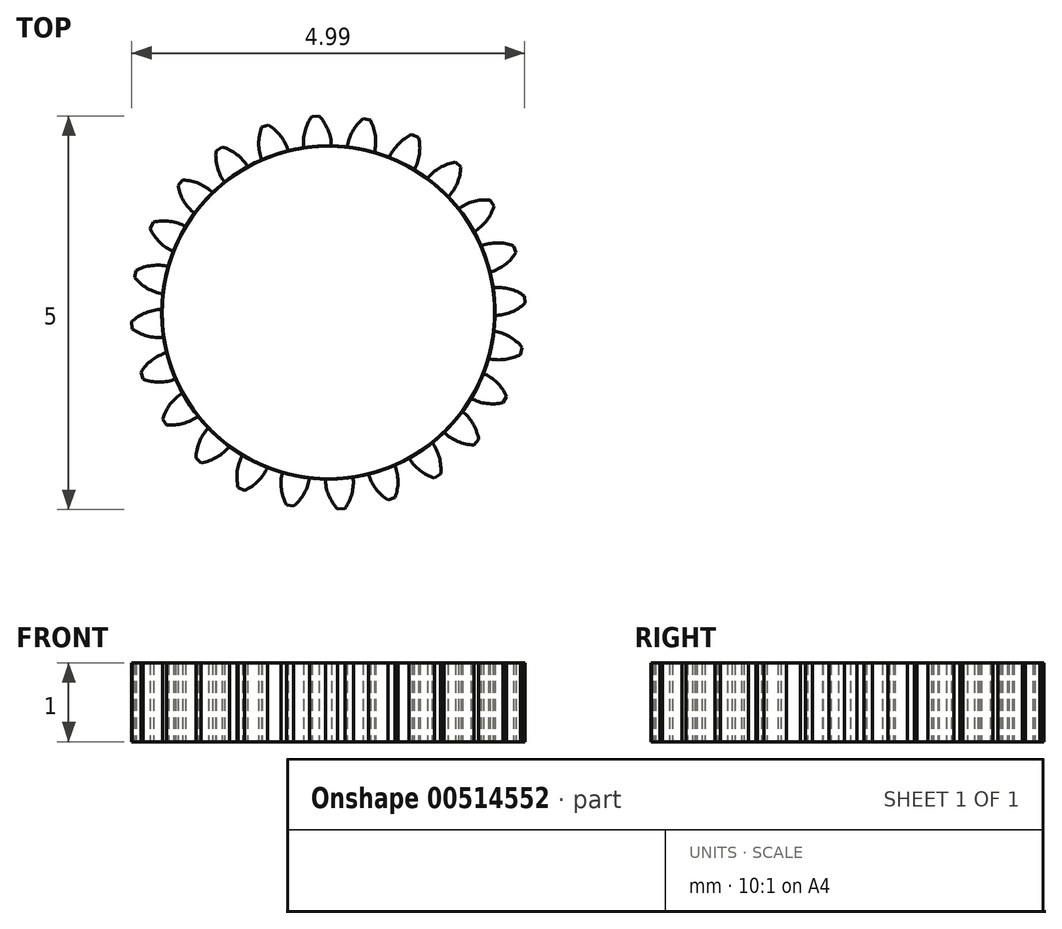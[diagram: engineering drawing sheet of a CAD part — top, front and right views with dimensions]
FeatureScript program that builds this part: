
annotation { "Feature Type Name" : "Feature", "Feature Type Description" : "" }
export const myFeature = defineFeature(function(context is Context, id is Id, definition is map)
    precondition{}
    {
        {
            var Q0;
            Q0=qCreatedBy(makeId("Top.planeOp"),FACE);
            var sketch = newSketch(context, id + "F0", { "sketchPlane" : qUnion([Q0])});
            skCircle(sketch, "E0", {"center": v(-6.84, 1.37) * mm, "radius": 2.12 * mm});
            skCircle(sketch, "E1", {"center": v(-6.84, 1.37) * mm, "radius": 2.31 * mm, "construction": true});
            skCircle(sketch, "E2", {"center": v(-6.84, 1.37) * mm, "radius": 2.5 * mm, "construction": true});
            skLineSegment(sketch, "E3", {"start": v(-6.84, 1.37) * mm, "end": v(-6.84, 4.9) * mm, "construction": true});
            skLineSegment(sketch, "E4", {"start": v(-6.84, 1.37) * mm, "end": v(-7.08, 4.96) * mm, "construction": true});
            skLineSegment(sketch, "E5", {"start": v(-6.84, 3.68) * mm, "end": v(-9.36, 3.68) * mm, "construction": true});
            skLineSegment(sketch, "E6", {"start": v(-6.84, 3.68) * mm, "end": v(-9.8, 2.6) * mm, "construction": true});
            skCircle(sketch, "E7", {"center": v(-6.84, 3.68) * mm, "radius": 0.57 * mm, "construction": true});
            skCircle(sketch, "E8", {"center": v(-6.84, 1.37) * mm, "radius": 2.17 * mm, "construction": true});
            skCircle(sketch, "E9", {"center": v(-7.38, 3.48) * mm, "radius": 0.57 * mm, "construction": true});
            skArc(sketch, "E10", {"start": v(-6.84, 3.68) * mm, "mid": v(-6.9, 3.78) * mm, "end": v(-6.96, 3.87) * mm});
            skArc(sketch, "E11", {"start": v(-6.8, 3.49) * mm, "mid": v(-6.81, 3.59) * mm, "end": v(-6.84, 3.68) * mm});
            skArc(sketch, "E12.MirrorCS", {"start": v(-7.14, 3.66) * mm, "mid": v(-7.1, 3.77) * mm, "end": v(-7.05, 3.86) * mm});
            skArc(sketch, "E13.MirrorCS", {"start": v(-7.16, 3.46) * mm, "mid": v(-7.16, 3.56) * mm, "end": v(-7.14, 3.66) * mm});
            skLineSegment(sketch, "E14", {"start": v(-7.05, 3.86) * mm, "end": v(-6.96, 3.87) * mm});
            skSolve(sketch);
        }
        {
            var Q0;
            Q0 = qSketchRegion(id + "F0", true);
            extrude(context, id + "F1", {"entities" : qUnion([Q0]), "depth" : 1 * mm, "offsetDistance" : 25 * mm});
        }
        {
            var Q0;
            Q0=makeQuery(id+"F1.opExtrude","SWEPT_BODY",BODY,{"disambiguationData":[OSD([sQuery(id+"F0.wireOp",EDGE,"E0"),sQuery(id+"F0.wireOp",EDGE,"E10"),sQuery(id+"F0.wireOp",EDGE,"E11"),sQuery(id+"F0.wireOp",EDGE,"E12.MirrorCS"),sQuery(id+"F0.wireOp",EDGE,"E13.MirrorCS"),sQuery(id+"F0.wireOp",EDGE,"E14")])]});
            var Q1;
            Q1=makeQuery(id+"F1.opExtrude","SWEPT_FACE",FACE,{"disambiguationData":[OSD([sQuery(id+"F0.wireOp",EDGE,"E0")])]});
            circularPattern(context, id + "F2", {"entities" : qUnion([Q0]), "axis" : qUnion([Q1]), "angle" : 360 * degree, "instanceCount" : 24, "equalSpace" : true});
        }
    });
